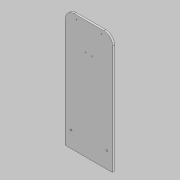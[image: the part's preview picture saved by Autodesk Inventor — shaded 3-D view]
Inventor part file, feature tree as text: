
AUTODESK INVENTOR PART (.ipt)
format: ipt  version: 2020 (Build 240168000, 168)  size: 115,200 bytes
history: native  units: in
note: dims shown in document units (in); Inventor stores cm internally (conversion verified against a paired STEP export)
features: sketch x3, fillet x2, hole x2, extrude x1
ambient origin geometry x8: Origin, YZ Plane, XZ Plane, XY Plane, X Axis, Y Axis, Z Axis, Center Point
bodies: Solid1 (feature_tree)
feature tree (8):
  extrude  "Extrusion1"  Depth=9.4488in
  fillet  "Fillet1"  Radius=4.7244in
  hole  "Hole1"  [1 undecoded]
  hole  "Hole2"  [1 undecoded]
  fillet  "Fillet2"  Radius=3.5433in
  sketch  "Sketch1"  dims[d0=23.622in d1=9.4488in d2=4.7244in]
  sketch  "Sketch2"  dims[d3=0.3937in d4=0.0in d5=1.7717in]
  sketch  "Sketch3"  dims[d8=3.2283in d9=3.2283in d10=0.315in d11=0.2362in d12=0.5512in d13=0.2756in d14=90.0deg d15=2.3622in d16=0.0in d17=3.5433in d18=3.5433in d19=0.6693in d20=0.6693in d21=2.5in d22=2.5in d23=0.7874in d24=0.7874in d25=4.7638in d26=4.7638in d27=0.1575in d28=0.2362in d29=0.1575in d30=0.0787in d31=90.0deg d32=0.315in d33=0.8108in d34=0.0787in]
note: 2 required parameter values undecoded (feature->parameter linkage not recoverable at this tier; creation-order binding heuristic only, values carry confidence <= 0.55)
